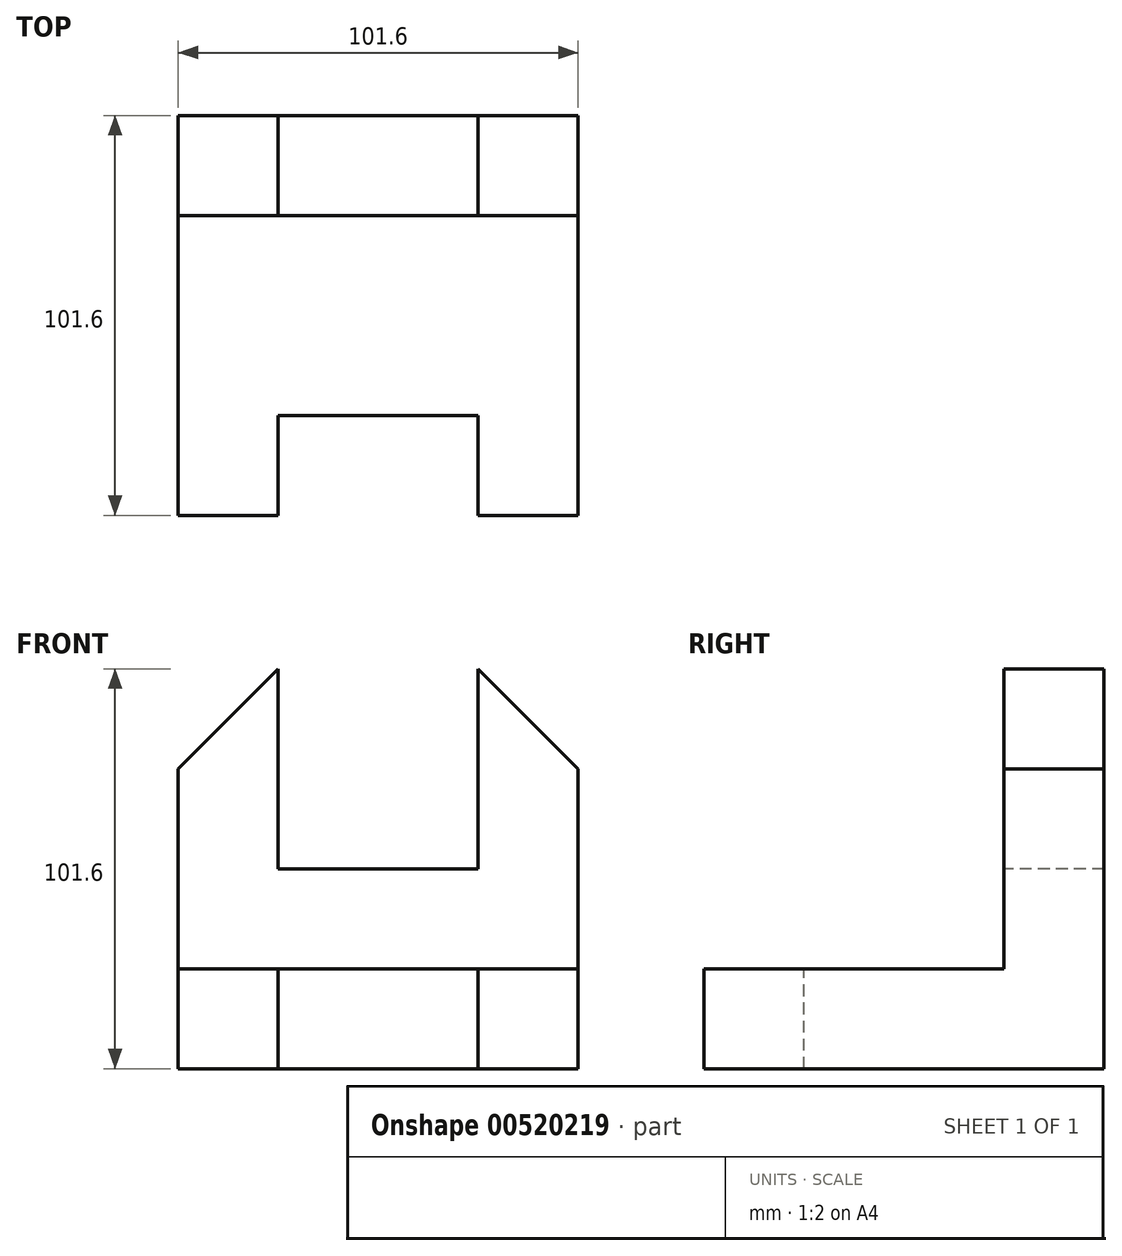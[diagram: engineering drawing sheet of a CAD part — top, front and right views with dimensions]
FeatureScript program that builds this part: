
annotation { "Feature Type Name" : "Feature", "Feature Type Description" : "" }
export const myFeature = defineFeature(function(context is Context, id is Id, definition is map)
    precondition{}
    {
        {
            var Q0;
            Q0=qCreatedBy(makeId("Front.planeOp"),FACE);
            var sketch = newSketch(context, id + "F0", { "sketchPlane" : qUnion([Q0])});
            skLineSegment(sketch, "E0.bottom", {"start": v(-56.62, 59.75) * mm, "end": v(44.98, 59.75) * mm});
            skLineSegment(sketch, "E0.top", {"start": v(-56.62, -41.85) * mm, "end": v(44.98, -41.85) * mm});
            skLineSegment(sketch, "E0.left", {"start": v(-56.62, 59.75) * mm, "end": v(-56.62, -41.85) * mm});
            skLineSegment(sketch, "E0.right", {"start": v(44.98, 59.75) * mm, "end": v(44.98, -41.85) * mm});
            skSolve(sketch);
        }
        {
            var Q0;
            Q0 = qSketchRegion(id + "F0", true);
            extrude(context, id + "F1", {"entities" : qUnion([Q0]), "depth" : 101.6 * mm, "offsetDistance" : 25.4 * mm});
        }
        {
            var Q0;
            Q0=makeQuery(id+"F1.opExtrude","CAP_FACE",FACE,{"disambiguationData":[OSD([sQuery(id+"F0.wireOp",EDGE,"E0.bottom"),sQuery(id+"F0.wireOp",EDGE,"E0.top"),sQuery(id+"F0.wireOp",EDGE,"E0.left"),sQuery(id+"F0.wireOp",EDGE,"E0.right")])],"isStart":false});
            var sketch = newSketch(context, id + "F2", { "sketchPlane" : qUnion([Q0])});
            skLineSegment(sketch, "E1", {"start": v(-31.22, -41.85) * mm, "end": v(19.58, -41.85) * mm});
            skLineSegment(sketch, "E2", {"start": v(19.58, -41.85) * mm, "end": v(44.98, -41.85) * mm});
            skLineSegment(sketch, "E3", {"start": v(-31.22, -41.85) * mm, "end": v(-31.22, -16.45) * mm});
            skLineSegment(sketch, "E4", {"start": v(-31.22, -16.45) * mm, "end": v(19.58, -16.45) * mm});
            skLineSegment(sketch, "E5", {"start": v(19.58, -16.45) * mm, "end": v(19.58, -41.85) * mm});
            skSolve(sketch);
        }
        {
            var Q0;
            Q0=makeQuery(id+"F2.imprint","IMPRINT",FACE,{"disambiguationData":[TD([[makeQuery(id+"F2.imprint","IMPRINT",EDGE,{"derivedFrom":sQuery(id+"F2.wireOp",EDGE,"E1")}),1.0]])]});
            extrude(context, id + "F3", {"entities" : qUnion([Q0]), "operationType" : NewBodyOperationType.REMOVE, "oppositeDirection" : true, "depth" : 25.4 * mm, "offsetDistance" : 25.4 * mm});
        }
        {
            var Q0;
            Q0=makeQuery(id+"F1.opExtrude","CAP_FACE",FACE,{"disambiguationData":[OSD([sQuery(id+"F0.wireOp",EDGE,"E0.bottom"),sQuery(id+"F0.wireOp",EDGE,"E0.top"),sQuery(id+"F0.wireOp",EDGE,"E0.left"),sQuery(id+"F0.wireOp",EDGE,"E0.right")])],"isStart":false});
            var sketch = newSketch(context, id + "F4", { "sketchPlane" : qUnion([Q0])});
            skLineSegment(sketch, "E6.bottom", {"start": v(-56.62, -16.45) * mm, "end": v(44.98, -16.45) * mm});
            skLineSegment(sketch, "E6.top", {"start": v(-56.62, 59.75) * mm, "end": v(44.98, 59.75) * mm});
            skLineSegment(sketch, "E6.left", {"start": v(-56.62, -16.45) * mm, "end": v(-56.62, 59.75) * mm});
            skLineSegment(sketch, "E6.right", {"start": v(44.98, -16.45) * mm, "end": v(44.98, 59.75) * mm});
            skSolve(sketch);
        }
        {
            var Q0;
            Q0 = qSketchRegion(id + "F4", true);
            extrude(context, id + "F5", {"entities" : qUnion([Q0]), "operationType" : NewBodyOperationType.REMOVE, "oppositeDirection" : true, "depth" : 76.2 * mm, "offsetDistance" : 25.4 * mm});
        }
        {
            var Q0;
            Q0=makeQuery(id+"F5.boolean.opBoolean","COPY",FACE,{"derivedFrom":makeQuery(id+"F5.opExtrude","CAP_FACE",FACE,{"disambiguationData":[OSD([sQuery(id+"F4.wireOp",EDGE,"E6.bottom"),sQuery(id+"F4.wireOp",EDGE,"E6.top"),sQuery(id+"F4.wireOp",EDGE,"E6.left"),sQuery(id+"F4.wireOp",EDGE,"E6.right")])],"isStart":false})});
            var sketch = newSketch(context, id + "F6", { "sketchPlane" : qUnion([Q0])});
            skLineSegment(sketch, "E7", {"start": v(-56.62, 59.75) * mm, "end": v(-31.22, 59.75) * mm});
            skLineSegment(sketch, "E8", {"start": v(-56.62, 59.75) * mm, "end": v(-56.62, 34.35) * mm});
            skLineSegment(sketch, "E9", {"start": v(-56.62, 34.35) * mm, "end": v(-31.22, 59.75) * mm});
            skLineSegment(sketch, "E10", {"start": v(19.58, 59.75) * mm, "end": v(44.98, 34.35) * mm});
            skLineSegment(sketch, "E11", {"start": v(44.98, 34.35) * mm, "end": v(44.98, 59.75) * mm});
            skLineSegment(sketch, "E12", {"start": v(44.98, 59.75) * mm, "end": v(19.58, 59.75) * mm});
            skSolve(sketch);
        }
        {
            var Q0;
            Q0=makeQuery(id+"F6.imprint","IMPRINT",FACE,{"disambiguationData":[TD([[makeQuery(id+"F6.imprint","IMPRINT",EDGE,{"derivedFrom":sQuery(id+"F6.wireOp",EDGE,"E10")}),1.0]])]});
            var Q1;
            Q1=makeQuery(id+"F6.imprint","IMPRINT",FACE,{"disambiguationData":[TD([[makeQuery(id+"F6.imprint","IMPRINT",EDGE,{"derivedFrom":sQuery(id+"F6.wireOp",EDGE,"E7")}),-1.0]])]});
            extrude(context, id + "F7", {"entities" : qUnion([Q0, Q1]), "operationType" : NewBodyOperationType.REMOVE, "oppositeDirection" : true, "depth" : 25.4 * mm, "offsetDistance" : 25.4 * mm});
        }
        {
            var Q0;
            Q0=makeQuery(id+"F5.boolean.opBoolean","COPY",FACE,{"derivedFrom":makeQuery(id+"F5.opExtrude","CAP_FACE",FACE,{"disambiguationData":[OSD([sQuery(id+"F4.wireOp",EDGE,"E6.bottom"),sQuery(id+"F4.wireOp",EDGE,"E6.top"),sQuery(id+"F4.wireOp",EDGE,"E6.left"),sQuery(id+"F4.wireOp",EDGE,"E6.right")])],"isStart":false})});
            var sketch = newSketch(context, id + "F8", { "sketchPlane" : qUnion([Q0])});
            skLineSegment(sketch, "E13.bottom", {"start": v(-31.22, 59.75) * mm, "end": v(19.58, 59.75) * mm});
            skLineSegment(sketch, "E13.top", {"start": v(-31.22, 8.95) * mm, "end": v(19.58, 8.95) * mm});
            skLineSegment(sketch, "E13.left", {"start": v(-31.22, 59.75) * mm, "end": v(-31.22, 8.95) * mm});
            skLineSegment(sketch, "E13.right", {"start": v(19.58, 59.75) * mm, "end": v(19.58, 8.95) * mm});
            skSolve(sketch);
        }
        {
            var Q0;
            Q0=makeQuery(id+"F8.imprint","IMPRINT",FACE,{"disambiguationData":[TD([[makeQuery(id+"F8.imprint","IMPRINT",EDGE,{"derivedFrom":sQuery(id+"F8.wireOp",EDGE,"E13.bottom")}),-1.0]])]});
            extrude(context, id + "F9", {"entities" : qUnion([Q0]), "operationType" : NewBodyOperationType.REMOVE, "oppositeDirection" : true, "depth" : 25.4 * mm, "offsetDistance" : 25.4 * mm});
        }
    });
